# Revit family: POOL 24W_LKB1257RGB.25
name_source: partatom
category: Luminarias
units: mm (PartAtom-declared; Revit-internal decimal feet)

## family parameters
Compartido = No
Corte con vacíos al cargar = No
Cota de conector redondo = Diámetro de uso
Origen de luz = Sí
Punto de cálculo de habitación = No
Se basa en plano de trabajo = Sí
Siempre vertical = No
Tipo de pieza = Normal

## types (1)
- SUB_LKB1257RGB.25
    Archivo de red fotométrica = LKB1257RGB.IES
    Cambio de temperatura de color de luz atenuada = <Ninguno>
    Carga aparente = 0 VA
    Comentarios de vataje = 24V
    Descripción = LUMINARIA SUB ACUATICA TIPO PUNTUAL PARA EMPOTRAR EN PISO 205MM DE DIAMETRO POR 126MM DE ALTO CONSIDERANDO EL HOUSING, ACABADO EN ACERO INOXIDABLE, CUERPO MOLDEADO EN CROMO, SELLO DE SILICON, VIDRIO TEMPLADO DE 9MM, 12 LED TIPO OSRAM CON UN CONSUMO TOTAL DE 33.6W, 805 LUMENES, RGB, IP 68, IK 08, SUMERGIBLE MAXIMO 2M, CABLE H07RN DE 3M, APERTURA EN STOCK A 25 GRADOS, ALIMENTADA A 24V. REQUIERE ACCESORIOS.
    Elevación por defecto = 0 mm  [stored 0 ft]
    Fabricante = BRILLANT
    Filtro de color = 16777215
    Lámpara = SMD3535 RGB
    Modelo = LKB1257RGB.25
    Watt per fixture = 33.6
    Ángulo de inclinación = 60.00°

note: [stored X ft] marks values corroborated as IEEE doubles in the binary element streams (Revit-internal decimal feet)

## geometry (parser evidence)
native form markers: Blend x2
no freeform markers — native parametric forms only
